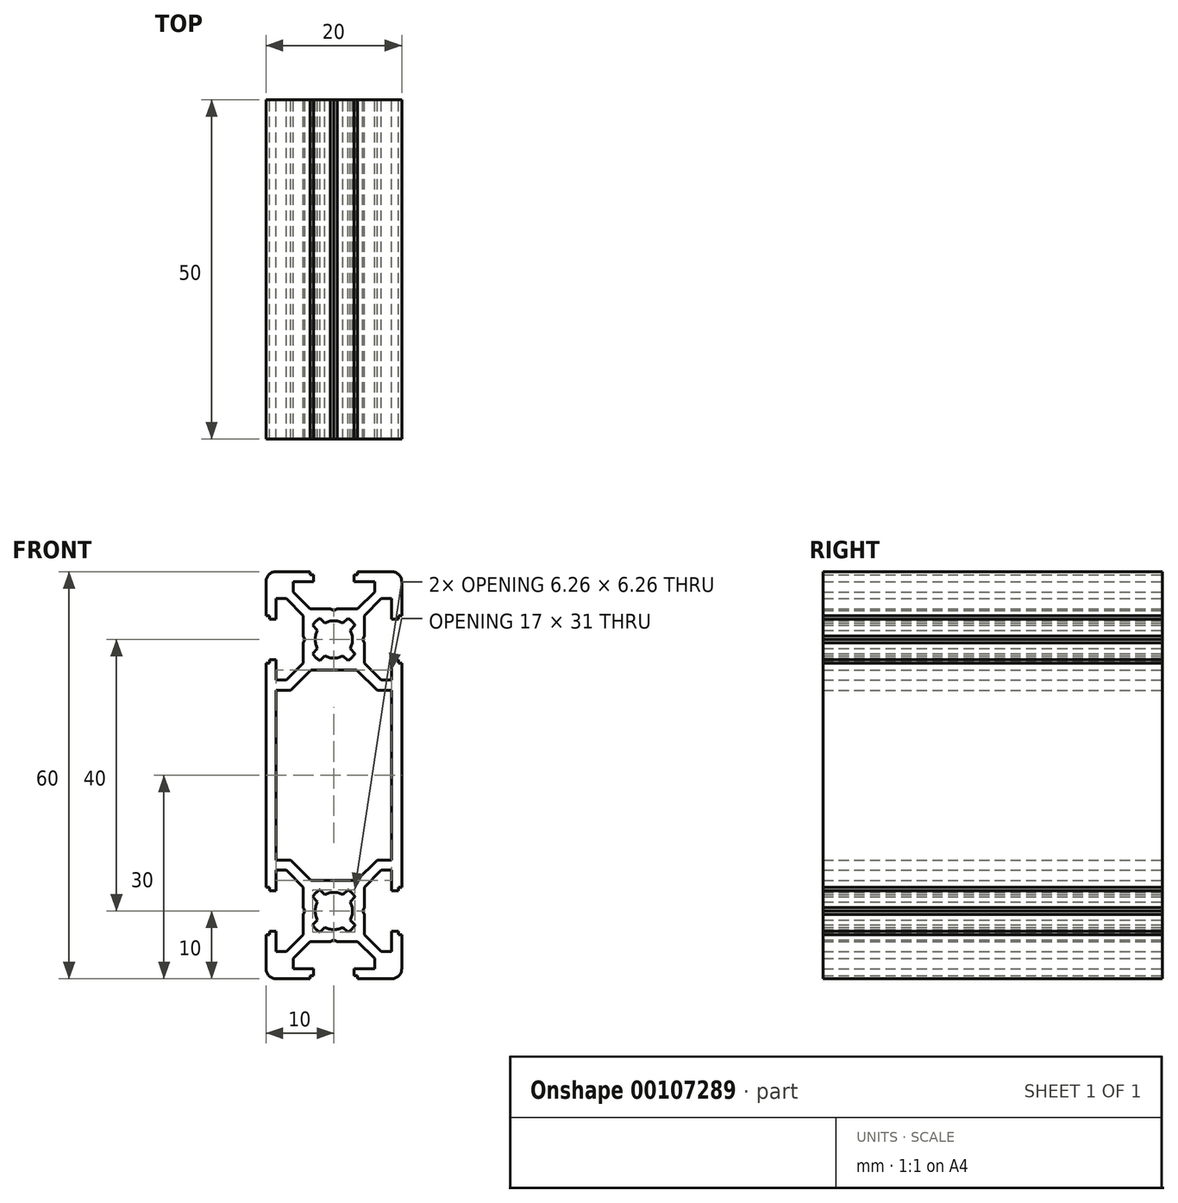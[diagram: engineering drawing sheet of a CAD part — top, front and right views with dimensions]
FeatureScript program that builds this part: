
annotation { "Feature Type Name" : "Feature", "Feature Type Description" : "" }
export const myFeature = defineFeature(function(context is Context, id is Id, definition is map)
    precondition{}
    {
        {
            var Q0;
            Q0=qCreatedBy(makeId("Front.planeOp"),FACE);
            var sketch = newSketch(context, id + "F0", { "sketchPlane" : qUnion([Q0])});
            skLineSegment(sketch, "E0.bottom", {"start": v(1.5, 0) * mm, "end": v(18.5, 0) * mm});
            skLineSegment(sketch, "E0.top", {"start": v(1.5, 60) * mm, "end": v(18.5, 60) * mm});
            skLineSegment(sketch, "E0.left", {"start": v(0, 1.5) * mm, "end": v(0, 58.5) * mm});
            skLineSegment(sketch, "E0.right", {"start": v(20, 1.5) * mm, "end": v(20, 58.5) * mm});
            skLineSegment(sketch, "E1", {"start": v(0, 30) * mm, "end": v(20, 30) * mm, "construction": true});
            skLineSegment(sketch, "E2", {"start": v(10, 60) * mm, "end": v(10, 0) * mm, "construction": true});
            skLineSegment(sketch, "E3", {"start": v(0, 60) * mm, "end": v(25.5, 34.5) * mm, "construction": true});
            skLineSegment(sketch, "E4", {"start": v(6.5, 60) * mm, "end": v(6.5, 59.5) * mm});
            skLineSegment(sketch, "E5", {"start": v(6.5, 59.5) * mm, "end": v(7, 59.5) * mm});
            skLineSegment(sketch, "E6", {"start": v(7, 59.5) * mm, "end": v(7, 58.5) * mm});
            skLineSegment(sketch, "E7", {"start": v(7, 58.5) * mm, "end": v(4, 58.5) * mm});
            skLineSegment(sketch, "E8", {"start": v(4, 58.5) * mm, "end": v(4, 57) * mm});
            skLineSegment(sketch, "E9", {"start": v(4, 57) * mm, "end": v(6.5, 54.5) * mm});
            skLineSegment(sketch, "E10", {"start": v(6.5, 54.5) * mm, "end": v(9.5, 54.5) * mm});
            skLineSegment(sketch, "E11", {"start": v(9.5, 54.5) * mm, "end": v(10, 54.25) * mm});
            skLineSegment(sketch, "E12.MirrorCS", {"start": v(10.5, 54.5) * mm, "end": v(10, 54.25) * mm});
            skLineSegment(sketch, "E13.MirrorCS", {"start": v(13.5, 54.5) * mm, "end": v(10.5, 54.5) * mm});
            skLineSegment(sketch, "E14.MirrorCS", {"start": v(16, 57) * mm, "end": v(13.5, 54.5) * mm});
            skLineSegment(sketch, "E15.MirrorCS", {"start": v(16, 58.5) * mm, "end": v(16, 57) * mm});
            skLineSegment(sketch, "E16.MirrorCS", {"start": v(13, 58.5) * mm, "end": v(16, 58.5) * mm});
            skLineSegment(sketch, "E17.MirrorCS", {"start": v(13, 59.5) * mm, "end": v(13, 58.5) * mm});
            skLineSegment(sketch, "E18.MirrorCS", {"start": v(13.5, 59.5) * mm, "end": v(13, 59.5) * mm});
            skLineSegment(sketch, "E19.MirrorCS", {"start": v(13.5, 60) * mm, "end": v(13.5, 59.5) * mm});
            skLineSegment(sketch, "E20.MirrorCS", {"start": v(0, 53.5) * mm, "end": v(0.5, 53.5) * mm});
            skLineSegment(sketch, "E21.MirrorCS", {"start": v(0.5, 53.5) * mm, "end": v(0.5, 53) * mm});
            skLineSegment(sketch, "E22.MirrorCS", {"start": v(0.5, 53) * mm, "end": v(1.5, 53) * mm});
            skLineSegment(sketch, "E23.MirrorCS", {"start": v(1.5, 53) * mm, "end": v(1.5, 56) * mm});
            skLineSegment(sketch, "E24.MirrorCS", {"start": v(1.5, 56) * mm, "end": v(3, 56) * mm});
            skLineSegment(sketch, "E25.MirrorCS", {"start": v(3, 56) * mm, "end": v(5.5, 53.5) * mm});
            skLineSegment(sketch, "E26.MirrorCS", {"start": v(5.5, 53.5) * mm, "end": v(5.5, 50.5) * mm});
            skLineSegment(sketch, "E27.MirrorCS", {"start": v(5.5, 50.5) * mm, "end": v(5.75, 50) * mm});
            skLineSegment(sketch, "E28.MirrorCS", {"start": v(5.5, 49.5) * mm, "end": v(5.75, 50) * mm});
            skLineSegment(sketch, "E29.MirrorCS", {"start": v(5.5, 46.5) * mm, "end": v(5.5, 49.5) * mm});
            skLineSegment(sketch, "E30.MirrorCS", {"start": v(3, 44) * mm, "end": v(5.5, 46.5) * mm});
            skLineSegment(sketch, "E31.MirrorCS", {"start": v(1.5, 44) * mm, "end": v(3, 44) * mm});
            skLineSegment(sketch, "E32.MirrorCS", {"start": v(1.5, 47) * mm, "end": v(1.5, 44) * mm});
            skLineSegment(sketch, "E33.MirrorCS", {"start": v(0.5, 47) * mm, "end": v(1.5, 47) * mm});
            skLineSegment(sketch, "E34.MirrorCS", {"start": v(0.5, 46.5) * mm, "end": v(0.5, 47) * mm});
            skLineSegment(sketch, "E35.MirrorCS", {"start": v(0, 46.5) * mm, "end": v(0.5, 46.5) * mm});
            skLineSegment(sketch, "E36.MirrorCS", {"start": v(20, 53.5) * mm, "end": v(19.5, 53.5) * mm});
            skLineSegment(sketch, "E37.MirrorCS", {"start": v(19.5, 53.5) * mm, "end": v(19.5, 53) * mm});
            skLineSegment(sketch, "E38.MirrorCS", {"start": v(19.5, 53) * mm, "end": v(18.5, 53) * mm});
            skLineSegment(sketch, "E39.MirrorCS", {"start": v(18.5, 53) * mm, "end": v(18.5, 56) * mm});
            skLineSegment(sketch, "E40.MirrorCS", {"start": v(18.5, 56) * mm, "end": v(17, 56) * mm});
            skLineSegment(sketch, "E41.MirrorCS", {"start": v(17, 56) * mm, "end": v(14.5, 53.5) * mm});
            skLineSegment(sketch, "E42.MirrorCS", {"start": v(14.5, 53.5) * mm, "end": v(14.5, 50.5) * mm});
            skLineSegment(sketch, "E43.MirrorCS", {"start": v(14.5, 50.5) * mm, "end": v(14.25, 50) * mm});
            skLineSegment(sketch, "E44.MirrorCS", {"start": v(14.5, 49.5) * mm, "end": v(14.25, 50) * mm});
            skLineSegment(sketch, "E45.MirrorCS", {"start": v(14.5, 46.5) * mm, "end": v(14.5, 49.5) * mm});
            skLineSegment(sketch, "E46.MirrorCS", {"start": v(17, 44) * mm, "end": v(14.5, 46.5) * mm});
            skLineSegment(sketch, "E47.MirrorCS", {"start": v(18.5, 44) * mm, "end": v(17, 44) * mm});
            skLineSegment(sketch, "E48.MirrorCS", {"start": v(18.5, 47) * mm, "end": v(18.5, 44) * mm});
            skLineSegment(sketch, "E49.MirrorCS", {"start": v(19.5, 47) * mm, "end": v(18.5, 47) * mm});
            skLineSegment(sketch, "E50.MirrorCS", {"start": v(19.5, 46.5) * mm, "end": v(19.5, 47) * mm});
            skLineSegment(sketch, "E51.MirrorCS", {"start": v(20, 46.5) * mm, "end": v(19.5, 46.5) * mm});
            skLineSegment(sketch, "E52.MirrorCS", {"start": v(6.5, 0) * mm, "end": v(6.5, 0.5) * mm});
            skLineSegment(sketch, "E53.MirrorCS", {"start": v(6.5, 0.5) * mm, "end": v(7, 0.5) * mm});
            skLineSegment(sketch, "E54.MirrorCS", {"start": v(7, 0.5) * mm, "end": v(7, 1.5) * mm});
            skLineSegment(sketch, "E55.MirrorCS", {"start": v(7, 1.5) * mm, "end": v(4, 1.5) * mm});
            skLineSegment(sketch, "E56.MirrorCS", {"start": v(4, 1.5) * mm, "end": v(4, 3) * mm});
            skLineSegment(sketch, "E57.MirrorCS", {"start": v(4, 3) * mm, "end": v(6.5, 5.5) * mm});
            skLineSegment(sketch, "E58.MirrorCS", {"start": v(6.5, 5.5) * mm, "end": v(9.5, 5.5) * mm});
            skLineSegment(sketch, "E59.MirrorCS", {"start": v(9.5, 5.5) * mm, "end": v(10, 5.75) * mm});
            skLineSegment(sketch, "E60.MirrorCS", {"start": v(10.5, 5.5) * mm, "end": v(10, 5.75) * mm});
            skLineSegment(sketch, "E61.MirrorCS", {"start": v(13.5, 5.5) * mm, "end": v(10.5, 5.5) * mm});
            skLineSegment(sketch, "E62.MirrorCS", {"start": v(16, 3) * mm, "end": v(13.5, 5.5) * mm});
            skLineSegment(sketch, "E63.MirrorCS", {"start": v(16, 1.5) * mm, "end": v(16, 3) * mm});
            skLineSegment(sketch, "E64.MirrorCS", {"start": v(13, 1.5) * mm, "end": v(16, 1.5) * mm});
            skLineSegment(sketch, "E65.MirrorCS", {"start": v(13, 0.5) * mm, "end": v(13, 1.5) * mm});
            skLineSegment(sketch, "E66.MirrorCS", {"start": v(13.5, 0.5) * mm, "end": v(13, 0.5) * mm});
            skLineSegment(sketch, "E67.MirrorCS", {"start": v(13.5, 0) * mm, "end": v(13.5, 0.5) * mm});
            skLineSegment(sketch, "E68.MirrorCS", {"start": v(0, 6.5) * mm, "end": v(0.5, 6.5) * mm});
            skLineSegment(sketch, "E69.MirrorCS", {"start": v(0.5, 6.5) * mm, "end": v(0.5, 7) * mm});
            skLineSegment(sketch, "E70.MirrorCS", {"start": v(0.5, 7) * mm, "end": v(1.5, 7) * mm});
            skLineSegment(sketch, "E71.MirrorCS", {"start": v(1.5, 7) * mm, "end": v(1.5, 4) * mm});
            skLineSegment(sketch, "E72.MirrorCS", {"start": v(1.5, 4) * mm, "end": v(3, 4) * mm});
            skLineSegment(sketch, "E73.MirrorCS", {"start": v(3, 4) * mm, "end": v(5.5, 6.5) * mm});
            skLineSegment(sketch, "E74.MirrorCS", {"start": v(5.5, 6.5) * mm, "end": v(5.5, 9.5) * mm});
            skLineSegment(sketch, "E75.MirrorCS", {"start": v(5.5, 9.5) * mm, "end": v(5.75, 10) * mm});
            skLineSegment(sketch, "E76.MirrorCS", {"start": v(5.5, 10.5) * mm, "end": v(5.75, 10) * mm});
            skLineSegment(sketch, "E77.MirrorCS", {"start": v(5.5, 13.5) * mm, "end": v(5.5, 10.5) * mm});
            skLineSegment(sketch, "E78.MirrorCS", {"start": v(3, 16) * mm, "end": v(5.5, 13.5) * mm});
            skLineSegment(sketch, "E79.MirrorCS", {"start": v(1.5, 16) * mm, "end": v(3, 16) * mm});
            skLineSegment(sketch, "E80.MirrorCS", {"start": v(1.5, 13) * mm, "end": v(1.5, 16) * mm});
            skLineSegment(sketch, "E81.MirrorCS", {"start": v(0.5, 13) * mm, "end": v(1.5, 13) * mm});
            skLineSegment(sketch, "E82.MirrorCS", {"start": v(0.5, 13.5) * mm, "end": v(0.5, 13) * mm});
            skLineSegment(sketch, "E83.MirrorCS", {"start": v(0, 13.5) * mm, "end": v(0.5, 13.5) * mm});
            skLineSegment(sketch, "E84.MirrorCS", {"start": v(20, 6.5) * mm, "end": v(19.5, 6.5) * mm});
            skLineSegment(sketch, "E85.MirrorCS", {"start": v(19.5, 6.5) * mm, "end": v(19.5, 7) * mm});
            skLineSegment(sketch, "E86.MirrorCS", {"start": v(19.5, 7) * mm, "end": v(18.5, 7) * mm});
            skLineSegment(sketch, "E87.MirrorCS", {"start": v(18.5, 7) * mm, "end": v(18.5, 4) * mm});
            skLineSegment(sketch, "E88.MirrorCS", {"start": v(18.5, 4) * mm, "end": v(17, 4) * mm});
            skLineSegment(sketch, "E89.MirrorCS", {"start": v(17, 4) * mm, "end": v(14.5, 6.5) * mm});
            skLineSegment(sketch, "E90.MirrorCS", {"start": v(14.5, 6.5) * mm, "end": v(14.5, 9.5) * mm});
            skLineSegment(sketch, "E91.MirrorCS", {"start": v(14.5, 9.5) * mm, "end": v(14.25, 10) * mm});
            skLineSegment(sketch, "E92.MirrorCS", {"start": v(14.5, 10.5) * mm, "end": v(14.25, 10) * mm});
            skLineSegment(sketch, "E93.MirrorCS", {"start": v(14.5, 13.5) * mm, "end": v(14.5, 10.5) * mm});
            skLineSegment(sketch, "E94.MirrorCS", {"start": v(17, 16) * mm, "end": v(14.5, 13.5) * mm});
            skLineSegment(sketch, "E95.MirrorCS", {"start": v(18.5, 16) * mm, "end": v(17, 16) * mm});
            skLineSegment(sketch, "E96.MirrorCS", {"start": v(18.5, 13) * mm, "end": v(18.5, 16) * mm});
            skLineSegment(sketch, "E97.MirrorCS", {"start": v(19.5, 13) * mm, "end": v(18.5, 13) * mm});
            skLineSegment(sketch, "E98.MirrorCS", {"start": v(19.5, 13.5) * mm, "end": v(19.5, 13) * mm});
            skLineSegment(sketch, "E99.MirrorCS", {"start": v(20, 13.5) * mm, "end": v(19.5, 13.5) * mm});
            skPoint(sketch, "E100.visualSharp", {"position": v(0, 60) * mm});
            skArc(sketch, "E100.filletArc", {"start": v(1.5, 60) * mm, "mid": v(0.44, 59.56) * mm, "end": v(0, 58.5) * mm});
            skPoint(sketch, "E101.visualSharp", {"position": v(20, 60) * mm});
            skArc(sketch, "E101.filletArc", {"start": v(20, 58.5) * mm, "mid": v(19.56, 59.56) * mm, "end": v(18.5, 60) * mm});
            skPoint(sketch, "E102.visualSharp", {"position": v(20, 0) * mm});
            skArc(sketch, "E102.filletArc", {"start": v(18.5, 0) * mm, "mid": v(19.56, 0.44) * mm, "end": v(20, 1.5) * mm});
            skPoint(sketch, "E103.visualSharp", {"position": v(0, 0) * mm});
            skArc(sketch, "E103.filletArc", {"start": v(0, 1.5) * mm, "mid": v(0.44, 0.44) * mm, "end": v(1.5, 0) * mm});
            skArc(sketch, "E104", {"start": v(11.34, 52.4) * mm, "mid": v(10, 52.75) * mm, "end": v(8.66, 52.4) * mm});
            skLineSegment(sketch, "E105.0", {"start": v(3.62, 42.5) * mm, "end": v(6.62, 45.5) * mm});
            skLineSegment(sketch, "E105.1", {"start": v(1.5, 42.5) * mm, "end": v(3.62, 42.5) * mm});
            skLineSegment(sketch, "E106", {"start": v(1.5, 42.5) * mm, "end": v(1.5, 30) * mm});
            skLineSegment(sketch, "E107", {"start": v(6.62, 45.5) * mm, "end": v(10, 45.5) * mm});
            skLineSegment(sketch, "E108.MirrorCS", {"start": v(18.5, 42.5) * mm, "end": v(18.5, 30) * mm});
            skLineSegment(sketch, "E109.MirrorCS", {"start": v(18.5, 42.5) * mm, "end": v(16.38, 42.5) * mm});
            skLineSegment(sketch, "E110.MirrorCS", {"start": v(16.38, 42.5) * mm, "end": v(13.38, 45.5) * mm});
            skLineSegment(sketch, "E111.MirrorCS", {"start": v(13.38, 45.5) * mm, "end": v(10, 45.5) * mm});
            skLineSegment(sketch, "E112.MirrorCS", {"start": v(1.5, 17.5) * mm, "end": v(1.5, 30) * mm});
            skLineSegment(sketch, "E113.MirrorCS", {"start": v(1.5, 17.5) * mm, "end": v(3.62, 17.5) * mm});
            skLineSegment(sketch, "E114.MirrorCS", {"start": v(3.62, 17.5) * mm, "end": v(6.62, 14.5) * mm});
            skLineSegment(sketch, "E115.MirrorCS", {"start": v(6.62, 14.5) * mm, "end": v(10, 14.5) * mm});
            skLineSegment(sketch, "E116.MirrorCS", {"start": v(13.38, 14.5) * mm, "end": v(10, 14.5) * mm});
            skLineSegment(sketch, "E117.MirrorCS", {"start": v(16.38, 17.5) * mm, "end": v(13.38, 14.5) * mm});
            skLineSegment(sketch, "E118.MirrorCS", {"start": v(18.5, 17.5) * mm, "end": v(16.38, 17.5) * mm});
            skLineSegment(sketch, "E119.MirrorCS", {"start": v(18.5, 17.5) * mm, "end": v(18.5, 30) * mm});
            skArc(sketch, "E120.0", {"start": v(7.93, 53.13) * mm, "mid": v(7.35, 52.65) * mm, "end": v(6.87, 52.07) * mm});
            skLineSegment(sketch, "E121", {"start": v(7.93, 53.13) * mm, "end": v(8.66, 52.4) * mm});
            skLineSegment(sketch, "E122.MirrorCS", {"start": v(6.87, 52.07) * mm, "end": v(7.6, 51.34) * mm});
            skLineSegment(sketch, "E123.1.0", {"start": v(6.87, 47.93) * mm, "end": v(7.6, 48.66) * mm});
            skLineSegment(sketch, "E123.1.1", {"start": v(7.93, 46.87) * mm, "end": v(8.66, 47.6) * mm});
            skLineSegment(sketch, "E123.2.0", {"start": v(12.07, 46.87) * mm, "end": v(11.34, 47.6) * mm});
            skLineSegment(sketch, "E123.2.1", {"start": v(13.13, 47.93) * mm, "end": v(12.4, 48.66) * mm});
            skLineSegment(sketch, "E123.3.0", {"start": v(13.13, 52.07) * mm, "end": v(12.4, 51.34) * mm});
            skLineSegment(sketch, "E123.3.1", {"start": v(12.07, 53.13) * mm, "end": v(11.34, 52.4) * mm});
            skArc(sketch, "E124.trimOffspring", {"start": v(6.87, 47.93) * mm, "mid": v(7.35, 47.35) * mm, "end": v(7.93, 46.87) * mm});
            skArc(sketch, "E125.trimOffspring", {"start": v(12.07, 46.87) * mm, "mid": v(12.65, 47.35) * mm, "end": v(13.13, 47.93) * mm});
            skArc(sketch, "E126.trimOffspring", {"start": v(13.13, 52.07) * mm, "mid": v(12.65, 52.65) * mm, "end": v(12.07, 53.13) * mm});
            skArc(sketch, "E127.trimOffspring", {"start": v(7.6, 51.34) * mm, "mid": v(7.25, 50) * mm, "end": v(7.6, 48.66) * mm});
            skArc(sketch, "E128.trimOffspring", {"start": v(8.66, 47.6) * mm, "mid": v(10, 47.25) * mm, "end": v(11.34, 47.6) * mm});
            skArc(sketch, "E129.trimOffspring", {"start": v(12.4, 48.66) * mm, "mid": v(12.75, 50) * mm, "end": v(12.4, 51.34) * mm});
            skArc(sketch, "E130.MirrorCS", {"start": v(7.93, 6.87) * mm, "mid": v(7.35, 7.35) * mm, "end": v(6.87, 7.93) * mm});
            skLineSegment(sketch, "E131.MirrorCS", {"start": v(7.93, 6.87) * mm, "end": v(8.66, 7.6) * mm});
            skArc(sketch, "E132.MirrorCS", {"start": v(11.34, 7.6) * mm, "mid": v(10, 7.25) * mm, "end": v(8.66, 7.6) * mm});
            skLineSegment(sketch, "E133.MirrorCS", {"start": v(12.07, 6.87) * mm, "end": v(11.34, 7.6) * mm});
            skArc(sketch, "E134.MirrorCS", {"start": v(13.13, 7.93) * mm, "mid": v(12.65, 7.35) * mm, "end": v(12.07, 6.87) * mm});
            skLineSegment(sketch, "E135.MirrorCS", {"start": v(13.13, 7.93) * mm, "end": v(12.4, 8.66) * mm});
            skArc(sketch, "E136.MirrorCS", {"start": v(12.4, 11.34) * mm, "mid": v(12.75, 10) * mm, "end": v(12.4, 8.66) * mm});
            skLineSegment(sketch, "E137.MirrorCS", {"start": v(13.13, 12.07) * mm, "end": v(12.4, 11.34) * mm});
            skArc(sketch, "E138.MirrorCS", {"start": v(12.07, 13.13) * mm, "mid": v(12.65, 12.65) * mm, "end": v(13.13, 12.07) * mm});
            skLineSegment(sketch, "E139.MirrorCS", {"start": v(12.07, 13.13) * mm, "end": v(11.34, 12.4) * mm});
            skArc(sketch, "E140.MirrorCS", {"start": v(8.66, 12.4) * mm, "mid": v(10, 12.75) * mm, "end": v(11.34, 12.4) * mm});
            skLineSegment(sketch, "E141.MirrorCS", {"start": v(7.93, 13.13) * mm, "end": v(8.66, 12.4) * mm});
            skArc(sketch, "E142.MirrorCS", {"start": v(6.87, 12.07) * mm, "mid": v(7.35, 12.65) * mm, "end": v(7.93, 13.13) * mm});
            skLineSegment(sketch, "E143.MirrorCS", {"start": v(6.87, 12.07) * mm, "end": v(7.6, 11.34) * mm});
            skArc(sketch, "E144.MirrorCS", {"start": v(7.6, 8.66) * mm, "mid": v(7.25, 10) * mm, "end": v(7.6, 11.34) * mm});
            skLineSegment(sketch, "E145.MirrorCS", {"start": v(6.87, 7.93) * mm, "end": v(7.6, 8.66) * mm});
            skSolve(sketch);
        }
        {
            var Q0;
            {var subQ12=sQuery(id+"F0.wireOp",EDGE,"E4");Q0=makeQuery(id+"F0.imprint","IMPRINT",FACE,{"disambiguationData":[TD([[makeQuery(id+"F0.imprint","IMPRINT",EDGE,{"derivedFrom":subQ12}),-1.0]])]});}
            extrude(context, id + "F1", {"entities" : qUnion([Q0]), "depth" : 50 * mm});
        }
    });
